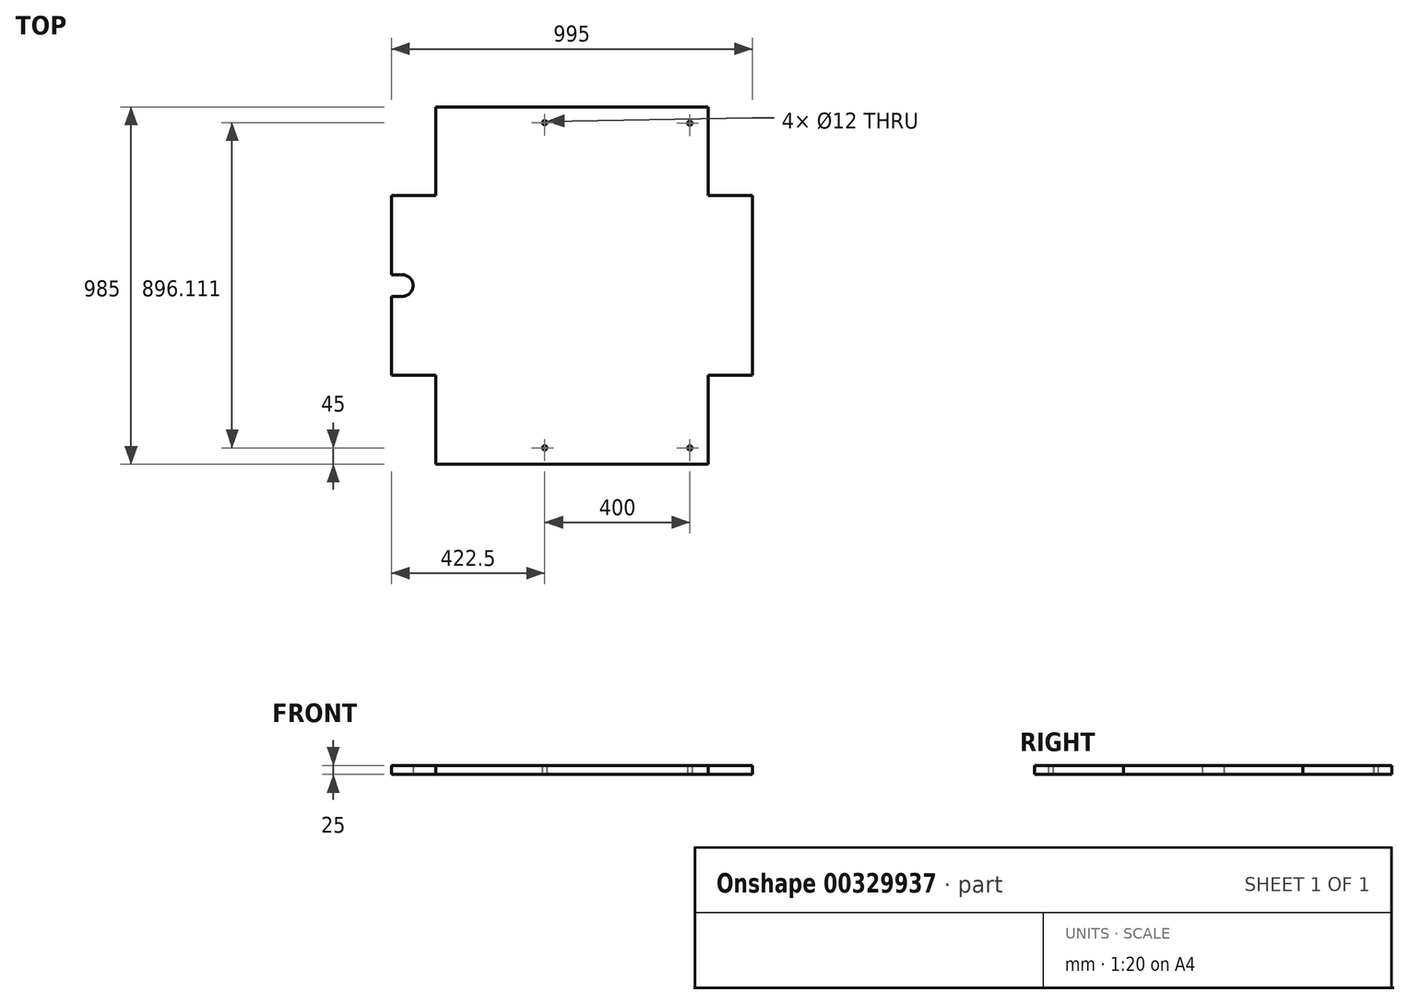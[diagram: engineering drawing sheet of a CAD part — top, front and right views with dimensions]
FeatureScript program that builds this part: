
annotation { "Feature Type Name" : "Feature", "Feature Type Description" : "" }
export const myFeature = defineFeature(function(context is Context, id is Id, definition is map)
    precondition{}
    {
        {
            var Q0;
            Q0=qCreatedBy(makeId("Top.planeOp"),FACE);
            var sketch = newSketch(context, id + "F0", { "sketchPlane" : qUnion([Q0])});
            skLineSegment(sketch, "E0.bottom", {"start": v(122.5, 0) * mm, "end": v(872.5, 0) * mm});
            skLineSegment(sketch, "E0.top", {"start": v(122.5, 985) * mm, "end": v(872.5, 985) * mm});
            skLineSegment(sketch, "E0.left", {"start": v(0, 245) * mm, "end": v(0, 462.5) * mm});
            skLineSegment(sketch, "E0.right", {"start": v(995, 245) * mm, "end": v(995, 740) * mm});
            skLineSegment(sketch, "E1", {"start": v(0, 740) * mm, "end": v(122.5, 740) * mm});
            skLineSegment(sketch, "E2", {"start": v(122.5, 740) * mm, "end": v(122.5, 985) * mm});
            skLineSegment(sketch, "E3", {"start": v(0, 245) * mm, "end": v(122.5, 245) * mm});
            skLineSegment(sketch, "E4", {"start": v(122.5, 245) * mm, "end": v(122.5, 0) * mm});
            skLineSegment(sketch, "E5", {"start": v(872.5, 985) * mm, "end": v(872.5, 740) * mm});
            skLineSegment(sketch, "E6", {"start": v(872.5, 740) * mm, "end": v(995, 740) * mm});
            skLineSegment(sketch, "E7", {"start": v(872.5, 0) * mm, "end": v(872.5, 245) * mm});
            skLineSegment(sketch, "E8", {"start": v(872.5, 245) * mm, "end": v(995, 245) * mm});
            skPoint(sketch, "E9", {"position": v(0, 492.5) * mm});
            skPoint(sketch, "E10", {"position": v(159.38, 492.5) * mm});
            skLineSegment(sketch, "E11", {"start": v(0, 522.5) * mm, "end": v(30, 522.5) * mm});
            skLineSegment(sketch, "E12", {"start": v(0, 462.5) * mm, "end": v(30, 462.5) * mm});
            skPoint(sketch, "E13", {"position": v(30, 492.5) * mm});
            skArc(sketch, "E14", {"start": v(30, 462.5) * mm, "mid": v(60, 492.5) * mm, "end": v(30, 522.5) * mm});
            skCircle(sketch, "E15", {"center": v(822.5, 940) * mm, "radius": 6 * mm});
            skCircle(sketch, "E16", {"center": v(422.5, 941.11) * mm, "radius": 6 * mm});
            skCircle(sketch, "E17", {"center": v(822.5, 45) * mm, "radius": 6 * mm});
            skCircle(sketch, "E18", {"center": v(422.5, 45) * mm, "radius": 6 * mm});
            skPoint(sketch, "E19.orphan", {"position": v(159.38, 462.5) * mm});
            skLineSegment(sketch, "E20.trimOffspring", {"start": v(0, 522.5) * mm, "end": v(0, 740) * mm});
            skPoint(sketch, "E21.orphan", {"position": v(0, 985) * mm});
            skPoint(sketch, "E22.orphan", {"position": v(0, 0) * mm});
            skSolve(sketch);
        }
        {
            var Q0;
            Q0 = qSketchRegion(id + "F0", true);
            extrude(context, id + "F1", {"entities" : qUnion([Q0]), "depth" : 25 * mm});
        }
    });
